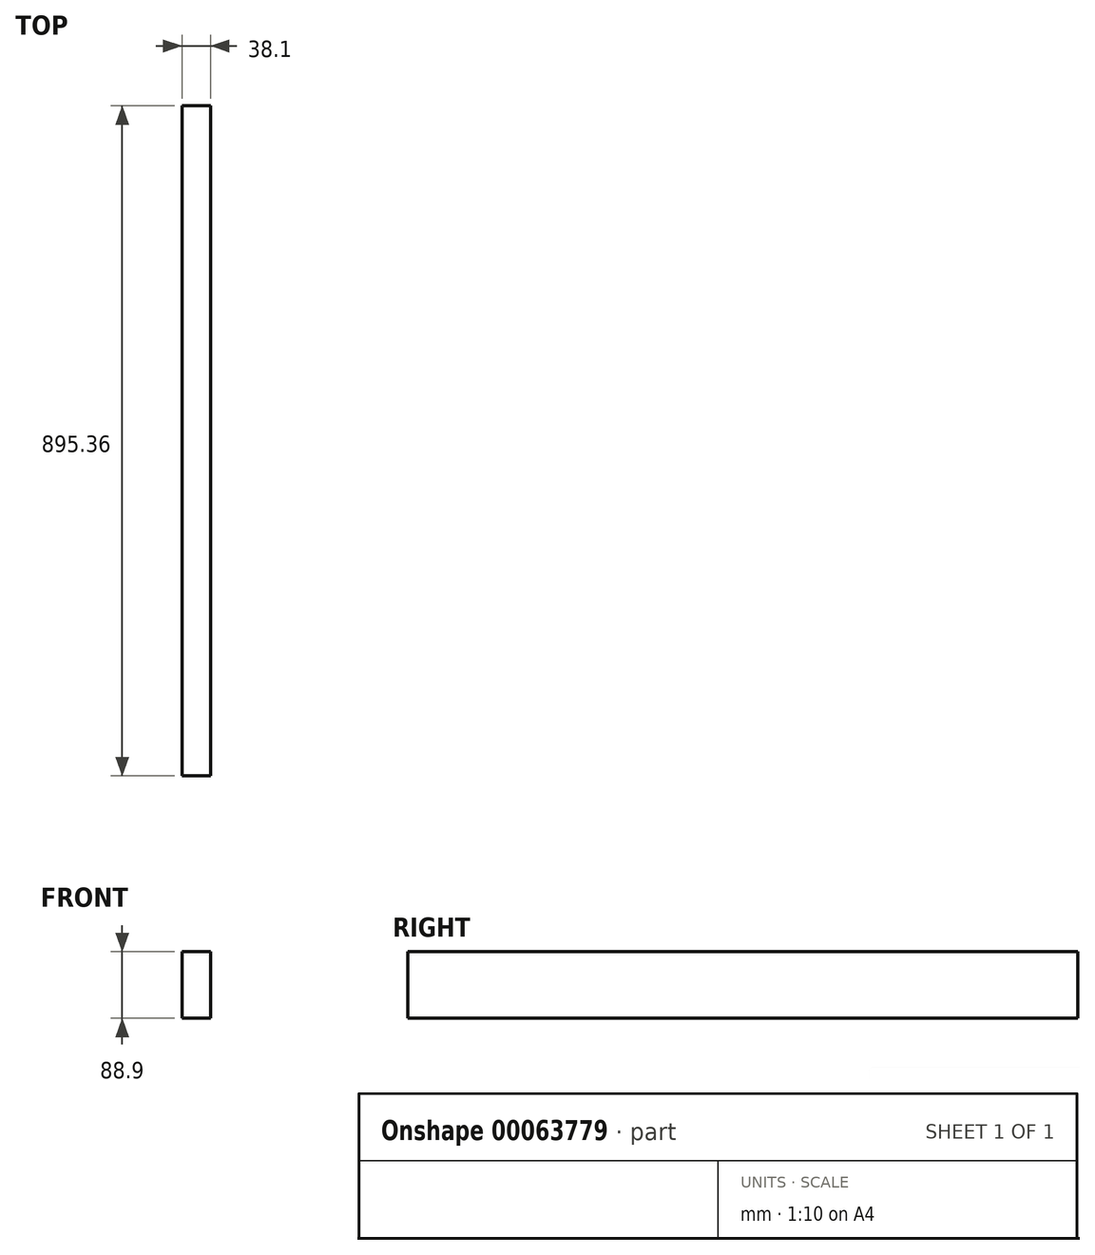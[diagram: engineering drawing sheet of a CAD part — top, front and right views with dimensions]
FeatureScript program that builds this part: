
annotation { "Feature Type Name" : "Feature", "Feature Type Description" : "" }
export const myFeature = defineFeature(function(context is Context, id is Id, definition is map)
    precondition{}
    {
        {
            var Q0;
            Q0=qCreatedBy(makeId("Front.planeOp"),FACE);
            var sketch = newSketch(context, id + "F0", { "sketchPlane" : qUnion([Q0])});
            skLineSegment(sketch, "E0.bottom", {"start": v(-18, 55.77) * mm, "end": v(20.1, 55.77) * mm});
            skLineSegment(sketch, "E0.top", {"start": v(-18, -33.13) * mm, "end": v(20.1, -33.13) * mm});
            skLineSegment(sketch, "E0.left", {"start": v(-18, 55.77) * mm, "end": v(-18, -33.13) * mm});
            skLineSegment(sketch, "E0.right", {"start": v(20.1, 55.77) * mm, "end": v(20.1, -33.13) * mm});
            skSolve(sketch);
        }
        {
            var Q0;
            Q0=qSketchRegion(id+"F0",true);
            extrude(context, id + "F1", {"entities" : qUnion([Q0]), "endBound" : BoundingType.SYMMETRIC, "depth" : 895.35 * mm});
        }
    });
